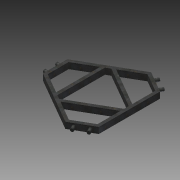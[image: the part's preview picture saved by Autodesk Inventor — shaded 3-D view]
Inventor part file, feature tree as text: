
AUTODESK INVENTOR PART (.ipt)
format: ipt  version: 2015 SP1 (Build 190203100, 203)  size: 155,648 bytes
history: native  units: in
note: dims shown in document units (in); Inventor stores cm internally (conversion verified against a paired STEP export)
features: extrude x4, sketch x4, projected_geometry x3
ambient origin geometry x8: Origin, YZ Plane, XZ Plane, XY Plane, X Axis, Y Axis, Z Axis, Center Point
bodies: Solid1 (feature_tree)
feature tree (11):
  extrude  "Extrusion1"  Depth=20.0in
  extrude  "Extrusion2"  Depth=15.5in
  extrude  "Extrusion3"  Depth=2.0in TaperAngle=0.0deg
  extrude  "Extrusion4"  Depth=2.0in
  sketch  "Sketch1"  dims[d0=8.0in d6=20.0in]
  sketch  "Sketch2"  dims[d14=15.5in d16=15.5in]
  projected_geometry  "Projected Loop1"
  sketch  "Sketch3"  dims[d17=15.5in d21=2.0in d22=0.0in]
  projected_geometry  "Projected Loop2"
  sketch  "Sketch4"  dims[d23=2.0in d24=2.0in d25=1.0in d26=1.0in d27=1.5in d28=0.0in d29=2.0in d30=2.0in d31=1.0in d32=1.0in d33=1.5in d34=0.0in d35=2.0in d36=2.0in d37=1.0in d38=1.0in d39=1.5in d40=0.0in]
  projected_geometry  "Projected Loop3"
